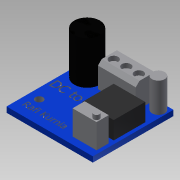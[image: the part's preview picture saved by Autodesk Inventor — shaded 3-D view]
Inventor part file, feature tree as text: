
AUTODESK INVENTOR PART (.ipt)
format: ipt  version: 2015 SP1 (Build 190203100, 203)  size: 512,000 bytes
history: native  units: mm
features: extrude x10, sketch x2, chamfer x1
ambient origin geometry x8: Origin, YZ Plane, XZ Plane, XY Plane, X Axis, Y Axis, Z Axis, Center Point
bodies: Solid1 (feature_tree)
feature tree (13):
  sketch  "Sketch1"  dims[d0=34.28mm d1=32.0mm]
  extrude  "Extrusion1"  Depth=32.0mm
  extrude  "Extrusion2"  Depth=4.05mm
  extrude  "Extrusion3"  Depth=8.95mm
  chamfer  "Chamfer1"  Distance=10.13mm
  extrude  "Extrusion4"  Depth=6.0mm
  extrude  "Extrusion5"  Depth=6.0mm
  extrude  "Extrusion6"  Depth=3.5mm
  extrude  "Extrusion7"  Depth=3.5mm
  extrude  "Extrusion8"  Depth=3.5mm
  extrude  "Extrusion9"  Depth=5.0mm
  extrude  "Extrusion10"  Depth=5.0mm
  sketch  "Sketch2"  dims[d2=3.0mm d3=4.05mm d4=8.95mm d5=10.13mm d6=6.0mm d7=6.0mm d8=3.5mm d9=3.5mm d10=3.5mm d11=5.0mm d12=5.0mm d13=5.0mm d14=3.0mm d15=3.0mm d16=12.5mm d17=12.5mm d18=15.0mm d19=7.5mm d20=2.0mm d21=9.53mm d22=4.82mm d23=1.330787mm d24=1.331mm d25=2.15mm d26=0.0mm d27=19.17mm d28=0.0mm d29=11.77mm d30=0.0mm d31=1.5mm d32=2.0mm d33=45.0deg d34=10.0mm d35=0.0mm d36=13.91mm d37=0.0mm d38=9.14mm d39=0.0mm d40=11.85mm d41=0.0mm d42=2.31mm d43=1.5mm d44=1.5mm d45=13.61mm d46=0.0mm d47=2.4mm d48=0.0mm d49=1.0mm d50=0.0mm]
